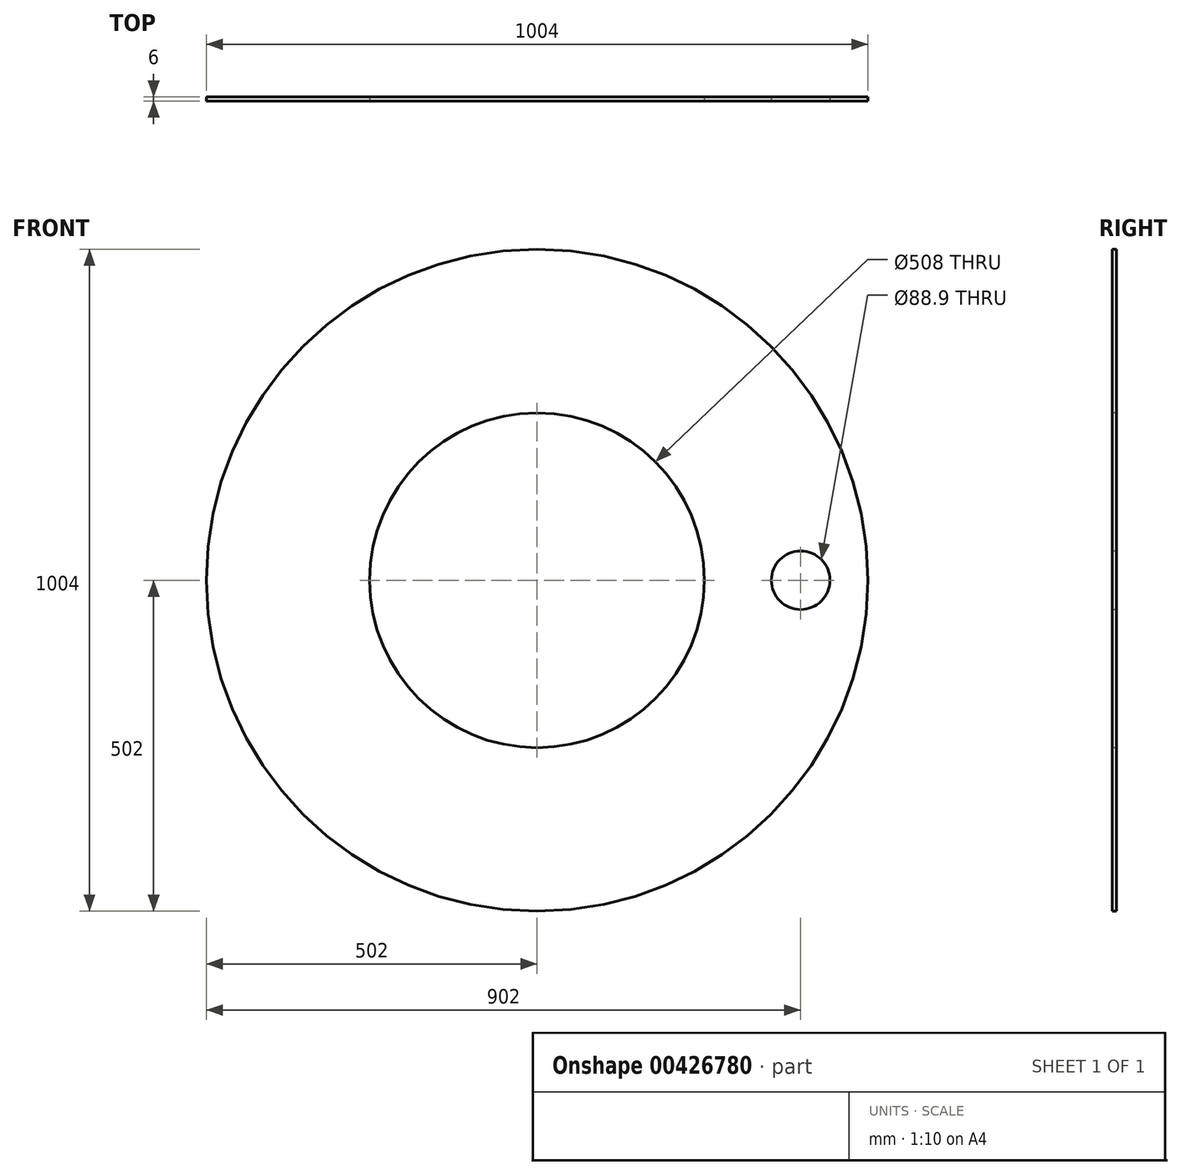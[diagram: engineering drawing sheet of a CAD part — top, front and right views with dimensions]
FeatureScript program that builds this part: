
annotation { "Feature Type Name" : "Feature", "Feature Type Description" : "" }
export const myFeature = defineFeature(function(context is Context, id is Id, definition is map)
    precondition{}
    {
        {
            var Q0;
            Q0=qCreatedBy(makeId("Front.planeOp"),FACE);
            var sketch = newSketch(context, id + "F0", { "sketchPlane" : qUnion([Q0])});
            skCircle(sketch, "E0", {"center": v(0, 0) * mm, "radius": 502 * mm});
            skCircle(sketch, "E1", {"center": v(0, 0) * mm, "radius": 254 * mm});
            skCircle(sketch, "E2", {"center": v(400, 0) * mm, "radius": 44.45 * mm});
            skSolve(sketch);
        }
        {
            var Q0;
            Q0=makeQuery(id+"F0.imprint","IMPRINT",FACE,{"disambiguationData":[TD([[makeQuery(id+"F0.imprint","IMPRINT",EDGE,{"derivedFrom":sQuery(id+"F0.wireOp",EDGE,"E0")}),1.0]])]});
            extrude(context, id + "F1", {"entities" : qUnion([Q0]), "oppositeDirection" : true, "depth" : 6 * mm});
        }
    });
